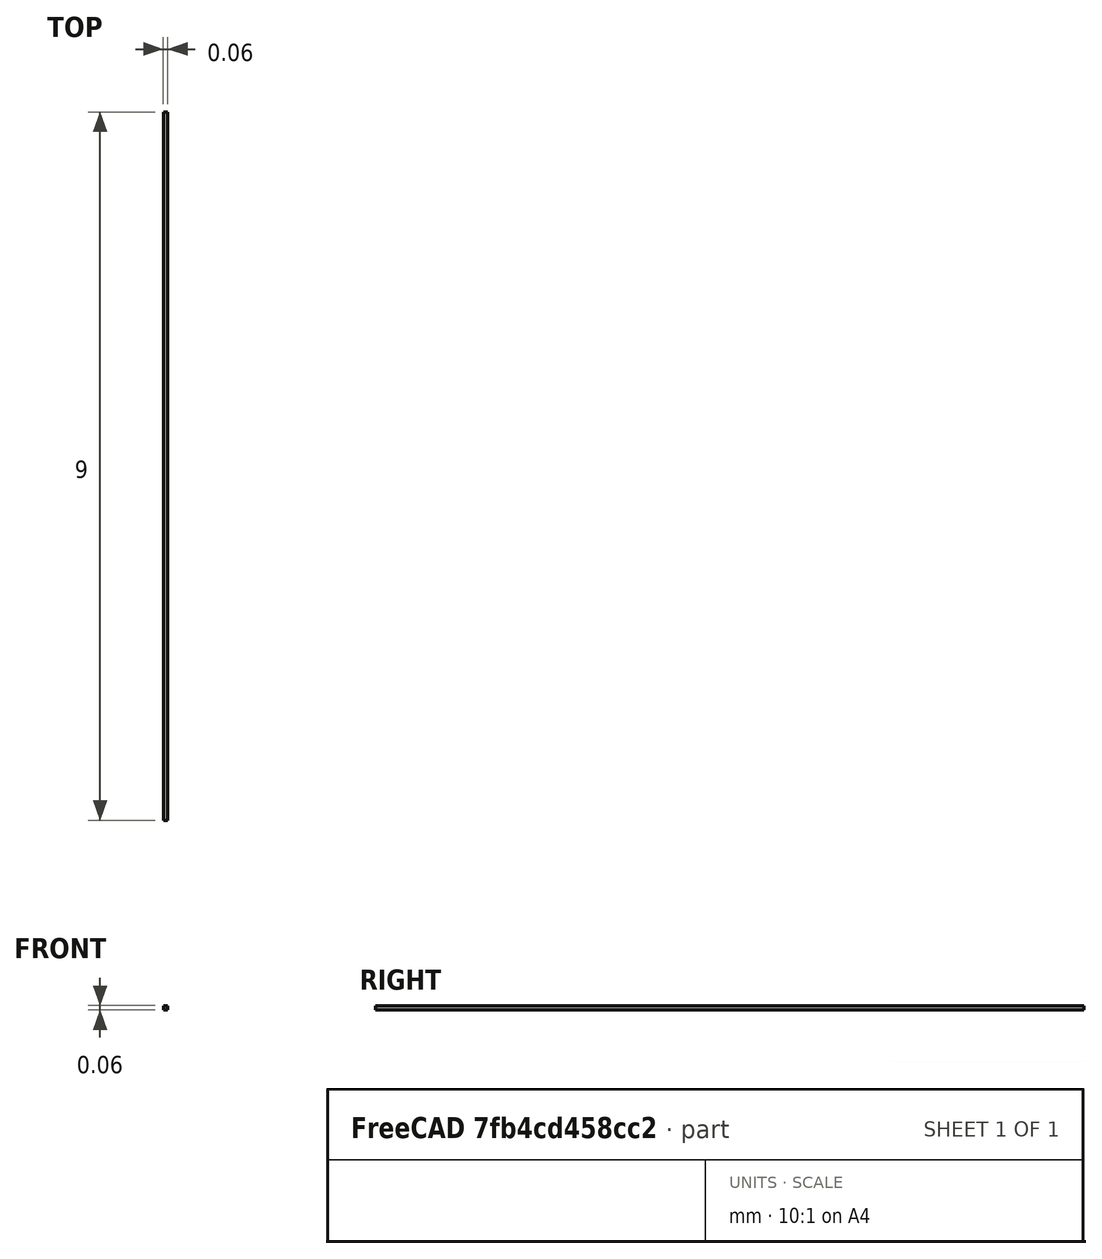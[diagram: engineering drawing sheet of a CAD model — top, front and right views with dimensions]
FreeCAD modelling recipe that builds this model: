
FCSTD DOCUMENT  (FreeCAD 0.16R6712 (Git))
Label: 1t
License: All rights reserved
LicenseURL: http://en.wikipedia.org/wiki/All_rights_reserved
objects: Sketcher::SketchObject×1, PartDesign::Pad×1, Mesh::Feature×1
note: 3 computed .brp shape members not serialized (recipe doc carries the construction recipe); baked Part::Feature solids carry a one-line shape summary decoded from their .brp

FEATURE [Sketcher::SketchObject] Sketch
  sketch-geometry (4):
    g0: LineSegment StartX=-0.025 StartY=0 StartZ=0 EndX=0.025 EndY=0 EndZ=0
    g1: LineSegment StartX=0.025 StartY=0 StartZ=0 EndX=0.025 EndY=9 EndZ=0
    g2: LineSegment StartX=0.025 StartY=9 StartZ=0 EndX=-0.025 EndY=9 EndZ=0
    g3: LineSegment StartX=-0.025 StartY=9 StartZ=0 EndX=-0.025 EndY=0 EndZ=0
  constraints (12):
    c: Coincident(g0,g1)
    c: Coincident(g1,g2)
    c: Coincident(g2,g3)
    c: Coincident(g3,g0)
    c: Horizontal(g0)
    c: Horizontal(g2)
    c: Vertical(g1)
    c: Vertical(g3)
    c: PointOnObject(g-1,g0)
    c: Distance(g1,g0) = 9
    c: Distance(g2,g1) = 0.05
    c: DistanceX(g-2,g0) = 0.025
FEATURE [PartDesign::Pad] Pad
  Length = 0.05
  Length2 = 100
  Midplane = true
  Sketch = -> Sketch
  Type = 0
FEATURE [Mesh::Feature] Mesh  label="Pad (Meshed)"
